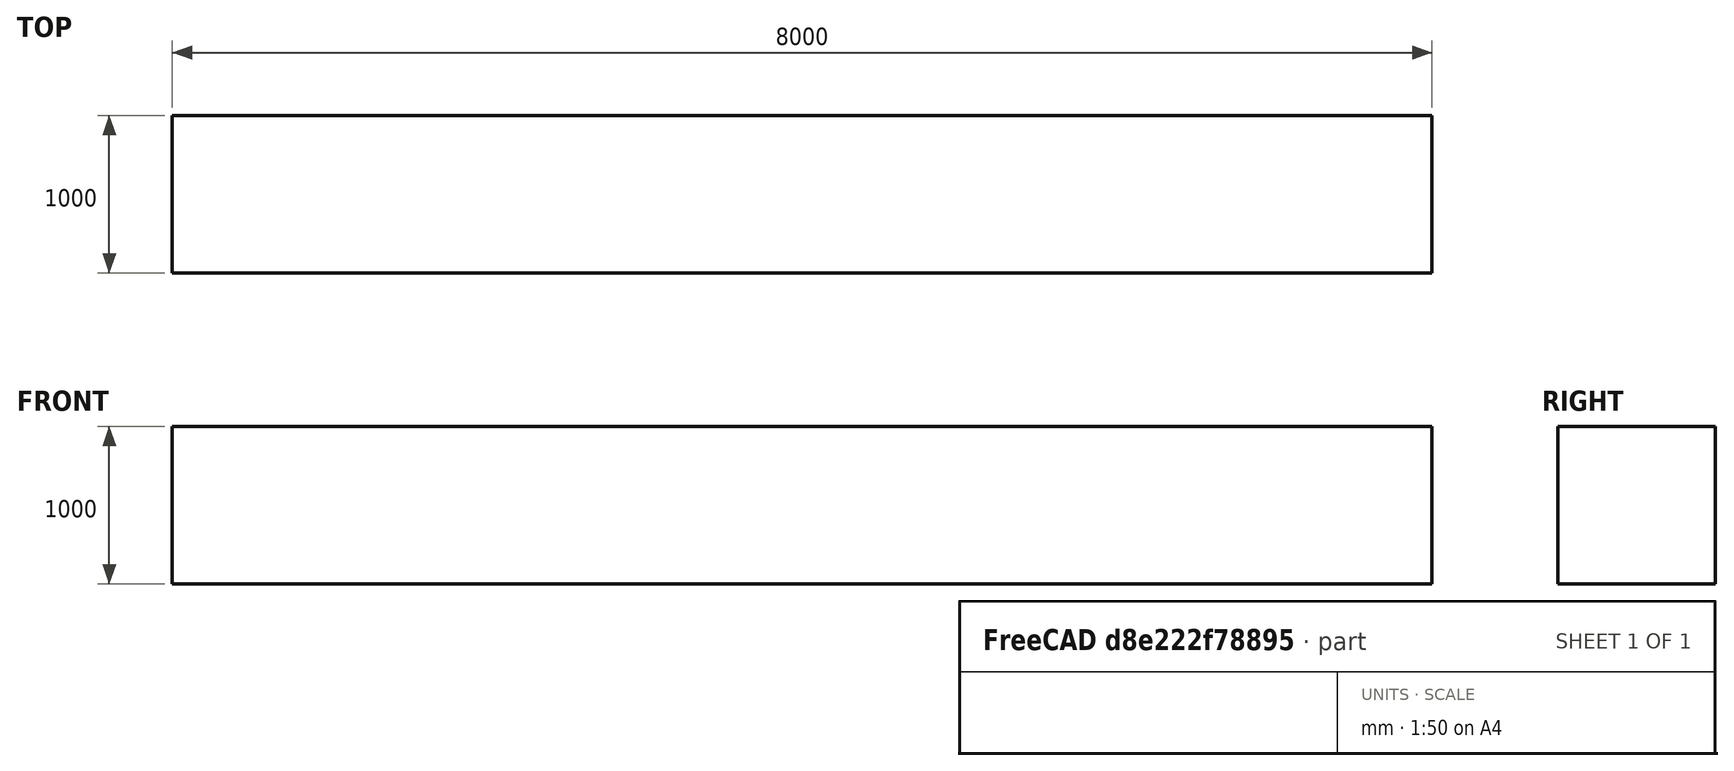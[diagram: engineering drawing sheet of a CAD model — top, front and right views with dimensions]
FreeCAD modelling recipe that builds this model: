
FCSTD DOCUMENT  (FreeCAD 0.19R20222 (Git))
Label: FemCalculixCantilever3D
License: CC-BY 3.0
LicenseURL: http://creativecommons.org/licenses/by/3.0/
objects: Part::Box×1, Fem::FemMeshShapeNetgenObject×1, Fem::ConstraintFixed×1, Fem::ConstraintForce×1, Fem::FemSolverObjectPython×1, Fem::FemPostWarpVectorFilter×1, Fem::FemPostPipeline×1, App::MaterialObjectPython×1, Fem::FemMeshObjectPython×1, Fem::FemResultObjectPython×1, Fem::FemAnalysis×1
note: 1 computed .brp shape members not serialized (recipe doc carries the construction recipe); baked Part::Feature solids carry a one-line shape summary decoded from their .brp

FEATURE [Part::Box] Box  label="Cube"
  AttacherType = Attacher::AttachEngine3D
  Height = 1000
  Length = 8000
  Width = 1000
FEATURE [Fem::FemMeshShapeNetgenObject] Box_Mesh
  Fineness = 2
  GrowthRate = 0.3
  MaxSize = 750
  NbSegsPerEdge = 1
  NbSegsPerRadius = 2
  Optimize = true
  SecondOrder = true
  Shape = -> Box
FEATURE [Fem::ConstraintFixed] FemConstraintFixed
  NormalDirection = (-1,0,0)
  Normals = (16) [(-1,0,0),(-1,0,0),(-1,0,0),(-1,0,0),(-1,0,0),(-1,0,0),(-1,0,0),(-1,0,0),(-1,0,0),(-1,0,0),(-1,0,0),(-1,0,0),(-1,0,0),(-1,0,0),(-1,0,0),(-1,0,0)]
  Points = (16) [(0,1000,0),(0,1000,333.333),(0,1000,666.667),(0,1000,1000),(0,666.667,0),(0,666.667,333.333),(0,666.667,666.667),(0,666.667,1000),(0,333.333,0),+7 more]
  References = -> [Box]
  Scale = 33
FEATURE [Fem::ConstraintForce] FemConstraintForce
  Direction = -> Box [Edge7]
  DirectionVector = (0,0,-1)
  Force = 9000000
  NormalDirection = (1,0,0)
  Points = (16) [(8000,1000,0),(8000,1000,333.333),(8000,1000,666.667),(8000,1000,1000),(8000,666.667,0),(8000,666.667,333.333),(8000,666.667,666.667),+9 more]
  References = -> [Box]
  Reversed = true
  Scale = 33
FEATURE [Fem::FemSolverObjectPython] CalculiXccxTools  # FEM object (typed FeaturePython)
  AnalysisType = 0
  BeamShellResultOutput3D = false
  EigenmodeHighLimit = 0
  EigenmodeLowLimit = 0
  EigenmodesCount = 15
  GeometricalNonlinearity = 0
  IterationsControlParameterCutb = 0.25,0.5,0.75,0.85,,,1.5,
  IterationsControlParameterIter = 4,8,9,200,10,400,,200,,
  IterationsControlParameterTimeUse = false
  IterationsThermoMechMaximum = 2000
  IterationsUserDefinedIncrementations = false
  IterationsUserDefinedTimeStepLength = false
  MaterialNonlinearity = 0
  MatrixSolverType = 0
  SplitInputWriter = false
  ThermoMechSteadyState = true
  TimeEnd = 1
  TimeInitialStep = 1
FEATURE [Fem::FemPostWarpVectorFilter] WarpVector
  Factor = 30
  Vector = 0
FEATURE [Fem::FemPostPipeline] Pipeline
  Filter = -> [WarpVector]
  Mode = 0
FEATURE [App::MaterialObjectPython] MechanicalSolidMaterial  # material (typed FeaturePython)
  Category = 0
  Material = AuthorAndLicense=CalculiX-Steel,CardName=CalculiX-Steel,Density=7900 kg/m^3,Description=Standard steel material for CalculiX sample calculations,+7 more (map truncated)
FEATURE [Fem::FemMeshObjectPython] ResultMesh  # FEM object (typed FeaturePython)
FEATURE [Fem::FemResultObjectPython] CCX_Results  # FEM object (typed FeaturePython)
  DisplacementLengths = [87.293,87.2919,87.2871,87.303,0,0,0,0,1.69117,4.749,9.48987,15.7836,23.4448,32.2894,42.1378,52.765,63.9816,75.6043,1.71227,4.76323,9.49458,15.7841,23.4563,32.3006,42.1436,52.7686,63.9856,75.605,1.69987,4.76597,9.50272,15.789,23.4497,32.3,+194 more]
  DisplacementVectors = (228) [(-8.12414,0.0331274,-86.9141),(8.10954,0.0194004,-86.9144),(-8.11693,0.0156184,-86.9089),(8.129,0.0338889,-86.9237),(0,0,0),(0,0,0),(0,0,0),(0,0,0),+220 more]
  Eigenmode = 0
  EigenmodeFrequency = 0
  MaxShear = [8.32303,12.233,7.81861,10.3501,145.45,166.254,164.198,159.367,195.261,175.602,159.398,137.991,115.471,98.0258,76.4131,56.444,40.0208,21.6838,208.492,173.445,153.762,137.795,119.111,97.0897,78.7785,56.35,36.4061,21.5611,209.671,179.108,+198 more]
  Mesh = -> ResultMesh
  NodeNumbers = [1,2,3,4,5,6,7,8,9,10,11,12,13,14,15,16,17,18,19,20,21,22,23,24,25,26,27,28,29,30,31,32,33,34,35,36,37,38,39,40,41,42,43,44,45,46,47,48,49,50,51,52,53,54,55,56,57,58,59,60,61,62,63,64,65,66,67,68,69,+159 more]
  NodeStrainXX = [-2.94247e-05,4.37605e-05,-4.06178e-05,6.77209e-05,-0.00160188,0.0017014,-0.00169713,0.00166628,0.00183225,0.00166858,0.00151396,0.00131144,0.0010913,0.00092362,0.00072007,0.000526737,0.000363372,0.000194506,0.00191949,0.00164746,0.00145956,+207 more]
  NodeStrainXY = [-5.11156e-06,7.60929e-06,8.667e-07,-5.81009e-06,0.000378376,-0.000261259,-0.000305502,0.00028564,-3.93768e-06,6.10543e-06,3.30471e-06,6.36125e-06,3.30347e-06,2.4686e-06,2.2419e-06,5.69935e-07,8.37956e-06,5.08079e-06,2.15865e-05,+209 more]
  NodeStrainXZ = [-4.44906e-05,-6.69567e-05,-3.88791e-05,-3.95426e-05,-0.000161419,-4.7972e-05,-0.000201415,5.52603e-06,-6.17784e-05,-7.72684e-05,-6.48202e-05,-4.42792e-05,-7.54524e-05,-7.18809e-05,-5.92929e-05,-6.51157e-05,-7.33054e-05,-4.83922e-05,+210 more]
  NodeStrainYY = [1.11828e-05,-1.47758e-05,2.38269e-05,-2.43765e-05,-1.71061e-09,-1.1311e-05,7.72706e-05,7.21717e-05,-0.000517687,-0.000502732,-0.00045451,-0.000395559,-0.000323878,-0.000284792,-0.000207615,-0.000156448,-0.000115706,-6.32254e-05,+210 more]
  NodeStrainYZ = [5.15517e-06,9.31756e-06,-5.42024e-06,-8.22508e-06,4.30682e-10,0.000133179,-0.000125466,-8.08658e-05,-1.59578e-05,-3.89722e-08,-1.11999e-06,-8.43081e-07,-2.2924e-06,-2.45923e-06,-7.3399e-07,-1.03684e-06,3.57769e-06,-2.558e-06,1.31756e-06,+209 more]
  NodeStrainZZ = [1.9671e-05,-2.07199e-05,1.30645e-05,-2.74203e-05,-2.11722e-09,-0.000255044,0.000173656,-0.000233901,-0.000578192,-0.000498363,-0.000454917,-0.000392945,-0.000329921,-0.000275767,-0.000218506,-0.000159748,-0.000104947,-5.39097e-05,+210 more]
  NodeStressXX = [-4.58009,8.0703,-7.0128,12.8688,-452.84,448.702,-449.365,451.449,385.194,350.408,317.805,275.203,229.292,193.186,151.932,110.596,75.9894,40.7939,393.458,346.823,307.164,274.932,236.208,192.967,157.644,112.129,71.5338,39.8516,-401.146,+199 more]
  NodeStressXY = [-0.825714,1.22919,0.140005,-0.938553,61.1223,-42.2034,-49.3503,46.1418,-0.636086,0.986261,0.533837,1.02759,0.533637,0.398774,0.362154,0.0920665,1.35362,0.820744,3.48704,-0.741721,-0.683296,-1.72221,-0.784733,-0.894264,-1.25392,-1.0729,+202 more]
  NodeStressXZ = [-7.18695,-10.8161,-6.28047,-6.38766,-26.0754,-7.74933,-32.5363,0.892667,-9.97959,-12.4818,-10.4709,-7.15279,-12.1885,-11.6115,-9.57808,-10.5187,-11.8416,-7.8172,-0.959316,-6.29468,-6.97194,-8.75984,-5.59937,-6.15981,-6.97177,-6.45882,+202 more]
  NodeStressYY = [1.97958,-1.38556,3.39749,-2.00846,-194.075,172.034,-162.731,193.94,5.58843,-0.342112,-0.178843,-0.542723,0.686253,-2.01872,2.07537,0.235452,-1.40007,-0.839584,-8.62688,1.74457,1.28623,-0.0236878,-1.1027,-0.346626,0.503836,0.179799,1.33735,+201 more]
  NodeStressYZ = [0.832758,1.50514,-0.875578,-1.32867,6.95716e-05,21.5135,-20.2676,-13.0629,-2.5778,-0.00629551,-0.180921,-0.13619,-0.37031,-0.397261,-0.118568,-0.167489,0.577935,-0.413216,0.212837,1.28089,1.19784,0.0237912,-0.837292,0.393826,-0.030194,+203 more]
  NodeStressZZ = [3.35076,-2.34576,1.65895,-2.50015,-194.075,132.662,-147.161,144.498,-4.18544,0.363619,-0.244579,-0.120373,-0.289787,-0.560865,0.316001,-0.297707,0.337838,0.665252,-23.4889,1.11159,0.899597,-0.0868691,-0.802949,-0.614813,0.799559,0.195623,+202 more]
  PrincipalMax = [7.81535,14.8705,5.32266,15.1879,-178.008,455.362,-133.229,459.473,385.45,350.855,318.15,275.393,229.939,193.88,152.536,111.585,77.8194,42.281,393.49,346.939,307.324,275.222,236.343,193.167,157.963,112.511,72.2043,41.4452,18.0432,-0.954298,+198 more]
  PrincipalMed = [1.76562,-0.936044,3.03554,-1.31536,-194.075,175.181,-164.402,189.675,6.21846,-0.0777822,-0.122591,-0.263706,0.753999,-1.10272,2.07833,0.251605,-0.669906,-0.574834,-8.65382,2.69086,2.22561,-0.0315865,-0.160371,-0.149212,0.577835,0.183066,+202 more]
  PrincipalMin = [-8.83072,-9.59547,-10.3146,-5.51233,-468.907,122.855,-461.626,140.739,-5.07193,-0.347987,-0.646098,-0.588942,-1.00414,-2.17119,-0.290546,-1.30288,-2.2223,-1.08662,-23.4944,0.0490315,-0.20006,-0.368479,-1.87995,-1.01228,0.406328,-0.189306,+202 more]
  ResultType = Fem::ResultMechanical
  Stats = [-8.13222,8.12992,-0.287103,0.295963,-86.9271,0,0,87.3065,11.6387,409.766,-186.44,470.561,-195.477,198.578,-468.907,191.365,6.25522,209.671,0,0,0,0,0,0,0,0]
  Time = 0
  vonMises = [14.5941,21.4874,14.6284,18.9535,283.208,309.678,313.973,297.302,385.001,351.068,318.535,275.819,230.069,195.519,151.656,112.119,79.2769,43.114,409.766,345.577,306.319,275.422,237.368,193.749,157.471,112.514,71.5676,42.4158,407.433,357.24,+198 more]
FEATURE [Fem::FemAnalysis] Analysis
  Group = -> [CalculiXccxTools,MechanicalSolidMaterial,FemConstraintFixed,FemConstraintForce,Box_Mesh,CCX_Results]
